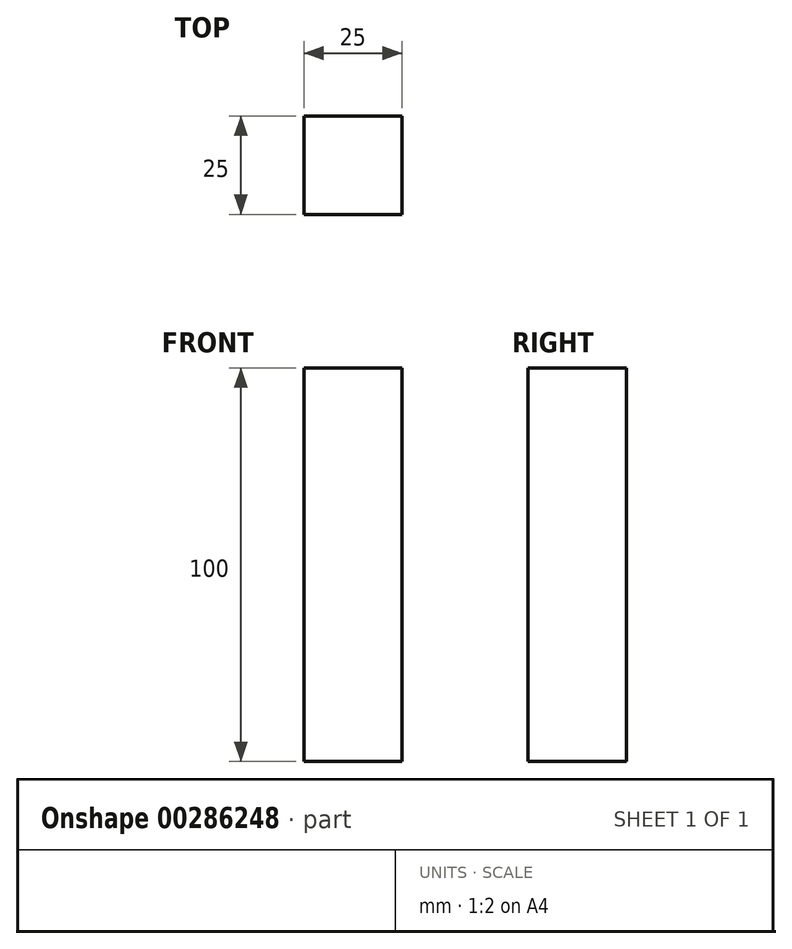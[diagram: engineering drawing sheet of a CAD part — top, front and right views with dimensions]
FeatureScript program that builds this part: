
annotation { "Feature Type Name" : "Feature", "Feature Type Description" : "" }
export const myFeature = defineFeature(function(context is Context, id is Id, definition is map)
    precondition{}
    {
        {
            var Q0;
            Q0=qCreatedBy(makeId("Front.planeOp"),FACE);
            var sketch = newSketch(context, id + "F0", { "sketchPlane" : qUnion([Q0])});
            skLineSegment(sketch, "E0.bottom", {"start": v(2.81, 0) * mm, "end": v(27.81, 0) * mm});
            skLineSegment(sketch, "E0.top", {"start": v(2.81, 100) * mm, "end": v(27.81, 100) * mm});
            skLineSegment(sketch, "E0.left", {"start": v(2.81, 0) * mm, "end": v(2.81, 100) * mm});
            skLineSegment(sketch, "E0.right", {"start": v(27.81, 0) * mm, "end": v(27.81, 100) * mm});
            skSolve(sketch);
        }
        {
            var Q0;
            Q0=qSketchRegion(id+"F0",true);
            extrude(context, id + "F1", {"entities" : qUnion([Q0]), "depth" : 25 * mm});
        }
    });
